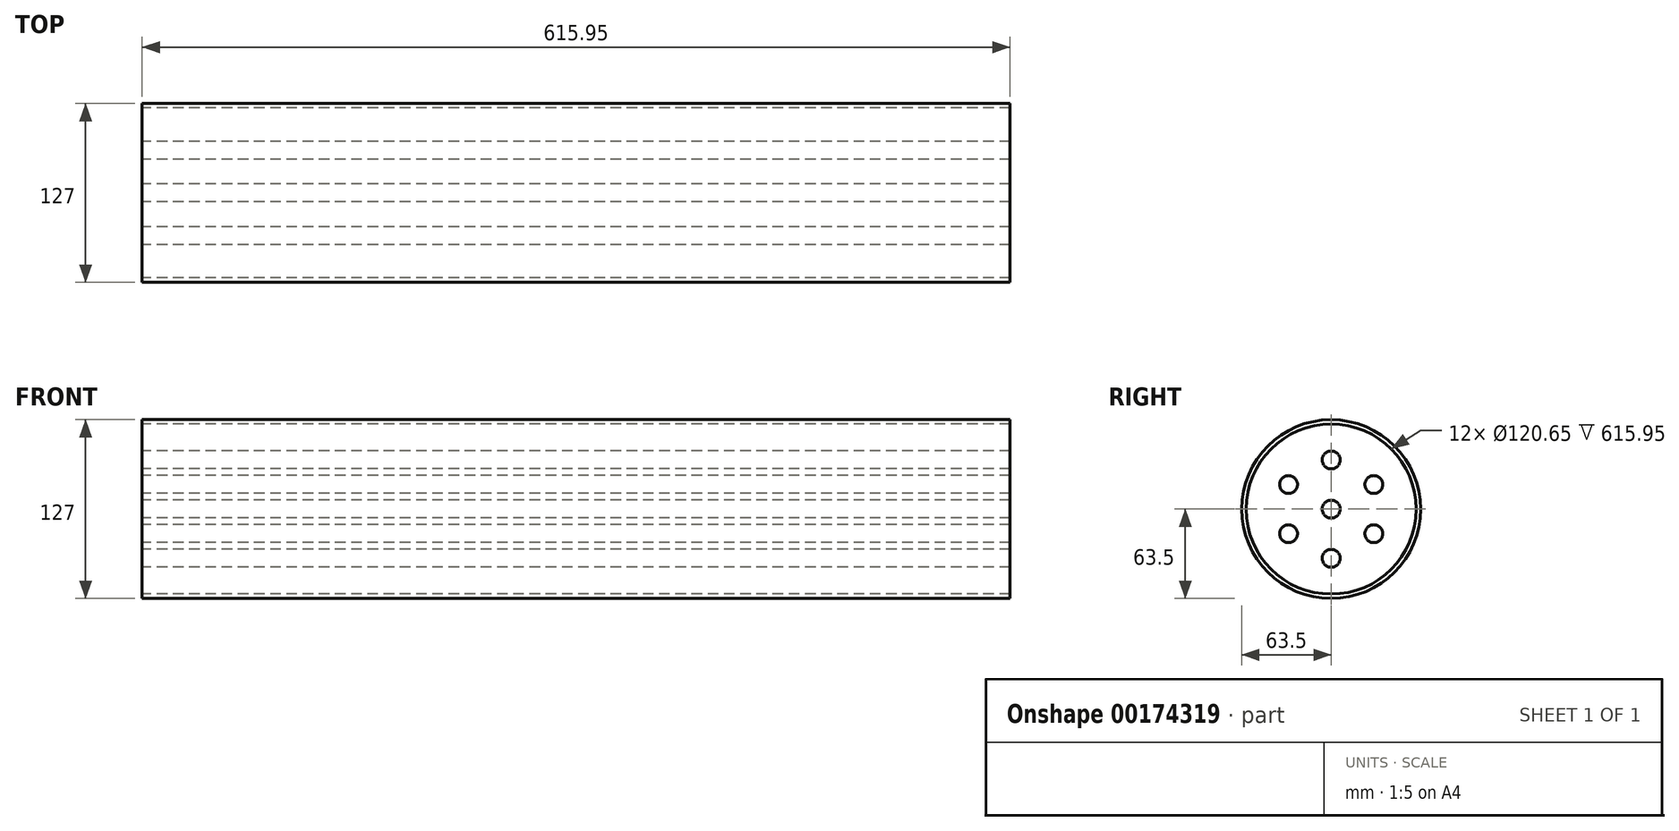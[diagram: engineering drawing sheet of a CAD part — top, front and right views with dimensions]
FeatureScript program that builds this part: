
annotation { "Feature Type Name" : "Feature", "Feature Type Description" : "" }
export const myFeature = defineFeature(function(context is Context, id is Id, definition is map)
    precondition{}
    {
        {
            var Q0;
            Q0=qCreatedBy(makeId("Right.planeOp"),FACE);
            var sketch = newSketch(context, id + "F0", { "sketchPlane" : qUnion([Q0])});
            skCircle(sketch, "E0", {"center": v(0, 0) * mm, "radius": 63.5 * mm});
            skCircle(sketch, "E1", {"center": v(0, 0) * mm, "radius": 60.33 * mm});
            skSolve(sketch);
        }
        {
            var Q0;
            Q0 = qSketchRegion(id + "F0", true);
            extrude(context, id + "F1", {"entities" : qUnion([Q0]), "depth" : 615.95 * mm});
        }
        {
            var Q0;
            Q0=qCreatedBy(makeId("Right.planeOp"),FACE);
            var sketch = newSketch(context, id + "F2", { "sketchPlane" : qUnion([Q0])});
            skCircle(sketch, "E2", {"center": v(0, 0) * mm, "radius": 6.35 * mm});
            skCircle(sketch, "E3", {"center": v(0, 34.93) * mm, "radius": 6.35 * mm});
            skCircle(sketch, "E4.1.0", {"center": v(-30.25, 17.46) * mm, "radius": 6.35 * mm});
            skCircle(sketch, "E4.2.0", {"center": v(-30.25, -17.46) * mm, "radius": 6.35 * mm});
            skCircle(sketch, "E4.3.0", {"center": v(0, -34.93) * mm, "radius": 6.35 * mm});
            skCircle(sketch, "E4.4.0", {"center": v(30.25, -17.46) * mm, "radius": 6.35 * mm});
            skCircle(sketch, "E4.5.0", {"center": v(30.25, 17.46) * mm, "radius": 6.35 * mm});
            skSolve(sketch);
        }
        {
            var Q0;
            Q0=makeQuery(id+"F2.imprint","IMPRINT",FACE,{"disambiguationData":[TD([[makeQuery(id+"F2.imprint","IMPRINT",EDGE,{"derivedFrom":sQuery(id+"F2.wireOp",EDGE,"E4.5.0")}),1.0]])]});
            var Q1;
            Q1=makeQuery(id+"F2.imprint","IMPRINT",FACE,{"disambiguationData":[TD([[makeQuery(id+"F2.imprint","IMPRINT",EDGE,{"derivedFrom":sQuery(id+"F2.wireOp",EDGE,"E3")}),1.0]])]});
            var Q2;
            Q2=makeQuery(id+"F2.imprint","IMPRINT",FACE,{"disambiguationData":[TD([[makeQuery(id+"F2.imprint","IMPRINT",EDGE,{"derivedFrom":sQuery(id+"F2.wireOp",EDGE,"E4.1.0")}),1.0]])]});
            var Q3;
            Q3=makeQuery(id+"F2.imprint","IMPRINT",FACE,{"disambiguationData":[TD([[makeQuery(id+"F2.imprint","IMPRINT",EDGE,{"derivedFrom":sQuery(id+"F2.wireOp",EDGE,"E4.2.0")}),1.0]])]});
            var Q4;
            Q4=makeQuery(id+"F2.imprint","IMPRINT",FACE,{"disambiguationData":[TD([[makeQuery(id+"F2.imprint","IMPRINT",EDGE,{"derivedFrom":sQuery(id+"F2.wireOp",EDGE,"E2")}),1.0]])]});
            var Q5;
            Q5=makeQuery(id+"F2.imprint","IMPRINT",FACE,{"disambiguationData":[TD([[makeQuery(id+"F2.imprint","IMPRINT",EDGE,{"derivedFrom":sQuery(id+"F2.wireOp",EDGE,"E4.4.0")}),1.0]])]});
            var Q6;
            Q6=makeQuery(id+"F2.imprint","IMPRINT",FACE,{"disambiguationData":[TD([[makeQuery(id+"F2.imprint","IMPRINT",EDGE,{"derivedFrom":sQuery(id+"F2.wireOp",EDGE,"E4.3.0")}),1.0]])]});
            extrude(context, id + "F3", {"entities" : qUnion([Q0, Q1, Q2, Q3, Q4, Q5, Q6]), "depth" : 615.95 * mm});
        }
    });
